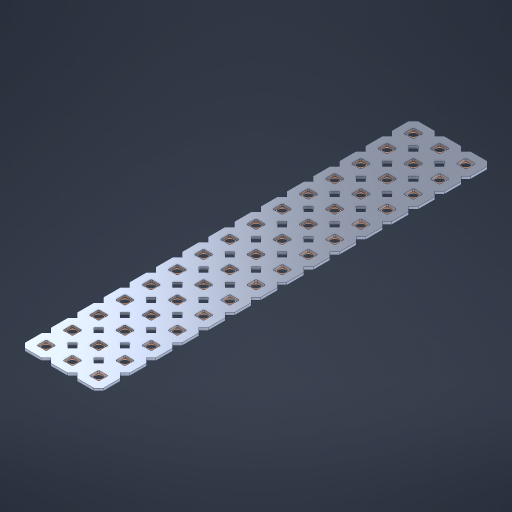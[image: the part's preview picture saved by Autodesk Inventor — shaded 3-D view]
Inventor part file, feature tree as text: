
AUTODESK INVENTOR PART (.ipt)
format: ipt  version: 2023 (Build 270158000, 158)  size: 780,800 bytes
history: native  units: in
note: dims shown in document units (in); Inventor stores cm internally (conversion verified against a paired STEP export)
features: other x46, extrude x44, sketch x2, pattern_linear x1
ambient origin geometry x8: Origin, YZ Plane, XZ Plane, XY Plane, X Axis, Y Axis, Z Axis, Center Point
bodies: Solid1 (feature_tree), Body (feature_tree)
feature tree (93):
  pattern_linear  "Rectangular Pattern1"  Spacing1=0.09in  [1 undecoded]
  sketch  "Sketch1"  dims[d1=0.5in]
  sketch  "Sketch2"  dims[d2=0.182in d3=0.09in d4=0.09in d5=0.09in d6=0.09in d7=0.09in d8=0.09in d9=0.09in d10=0.09in d11=0.02in d13=0.0in d14=0.172in d15=0.0625in d16=0.0in d19=0.5in d22=0.5in]
  other  "Srf1"
  other  "Srf126"
  other  "Srf127"
  other  "Srf128"
  other  "Srf129"
  other  "Srf130"
  other  "Srf131"
  other  "Srf250"
  other  "Srf251"
  other  "Srf252"
  other  "Srf253"
  other  "Srf254"
  other  "Srf255"
  other  "Srf256"
  other  "Srf257"
  other  "Srf268"
  other  "Srf269"
  other  "Srf270"
  other  "Srf271"
  other  "Srf272"
  other  "Srf273"
  other  "Srf274"
  other  "Srf275"
  other  "Srf276"
  other  "Srf277"
  other  "Srf278"
  other  "Srf279"
  other  "Srf280"
  other  "Srf281"
  other  "Srf282"
  other  "Srf293"
  other  "Srf294"
  other  "Srf295"
  other  "Srf296"
  other  "Srf297"
  other  "Srf298"
  other  "Srf299"
  other  "Srf300"
  other  "Srf301"
  other  "Srf302"
  other  "Srf303"
  other  "Srf304"
  other  "Srf305"
  other  "Srf306"
  other  "Srf307"
  other  "Circle"
  extrude  "ExtrusionSrf126"  Depth=0.09in
  extrude  "ExtrusionSrf127"  Depth=0.09in
  extrude  "ExtrusionSrf128"  Depth=0.09in
  extrude  "ExtrusionSrf129"  Depth=0.09in
  extrude  "ExtrusionSrf130"  Depth=0.09in
  extrude  "ExtrusionSrf131"  Depth=0.09in
  extrude  "ExtrusionSrf250"  Depth=0.09in
  extrude  "ExtrusionSrf251"  Depth=0.02in
  extrude  "ExtrusionSrf252"  TaperAngle=0.0deg  [1 undecoded]
  extrude  "ExtrusionSrf253"  Depth=0.5in
  extrude  "ExtrusionSrf254"  Depth=0.5in TaperAngle=0.0deg
  extrude  "ExtrusionSrf255"  Depth=0.5in
  extrude  "ExtrusionSrf256"  Depth=0.5in
  extrude  "ExtrusionSrf257"  [1 undecoded]
  extrude  "ExtrusionSrf268"  [1 undecoded]
  extrude  "ExtrusionSrf269"  [1 undecoded]
  extrude  "ExtrusionSrf270"  [1 undecoded]
  extrude  "ExtrusionSrf271"  [1 undecoded]
  extrude  "ExtrusionSrf272"  [1 undecoded]
  extrude  "ExtrusionSrf273"  [1 undecoded]
  extrude  "ExtrusionSrf274"  [1 undecoded]
  extrude  "ExtrusionSrf275"  [1 undecoded]
  extrude  "ExtrusionSrf276"  [1 undecoded]
  extrude  "ExtrusionSrf277"  [1 undecoded]
  extrude  "ExtrusionSrf278"  [1 undecoded]
  extrude  "ExtrusionSrf279"  [1 undecoded]
  extrude  "ExtrusionSrf280"  [1 undecoded]
  extrude  "ExtrusionSrf281"  [1 undecoded]
  extrude  "ExtrusionSrf282"  [1 undecoded]
  extrude  "ExtrusionSrf293"  [1 undecoded]
  extrude  "ExtrusionSrf294"  [1 undecoded]
  extrude  "ExtrusionSrf295"  [1 undecoded]
  extrude  "ExtrusionSrf296"  [1 undecoded]
  extrude  "ExtrusionSrf297"  [1 undecoded]
  extrude  "ExtrusionSrf298"  [1 undecoded]
  extrude  "ExtrusionSrf299"  [1 undecoded]
  extrude  "ExtrusionSrf300"  [1 undecoded]
  extrude  "ExtrusionSrf301"  [1 undecoded]
  extrude  "ExtrusionSrf302"  [1 undecoded]
  extrude  "ExtrusionSrf303"  [1 undecoded]
  extrude  "ExtrusionSrf304"  [1 undecoded]
  extrude  "ExtrusionSrf305"  [1 undecoded]
  extrude  "ExtrusionSrf306"  [1 undecoded]
  extrude  "ExtrusionSrf307"  [1 undecoded]
note: 33 required parameter values undecoded (feature->parameter linkage not recoverable at this tier; creation-order binding heuristic only, values carry confidence <= 0.55)
